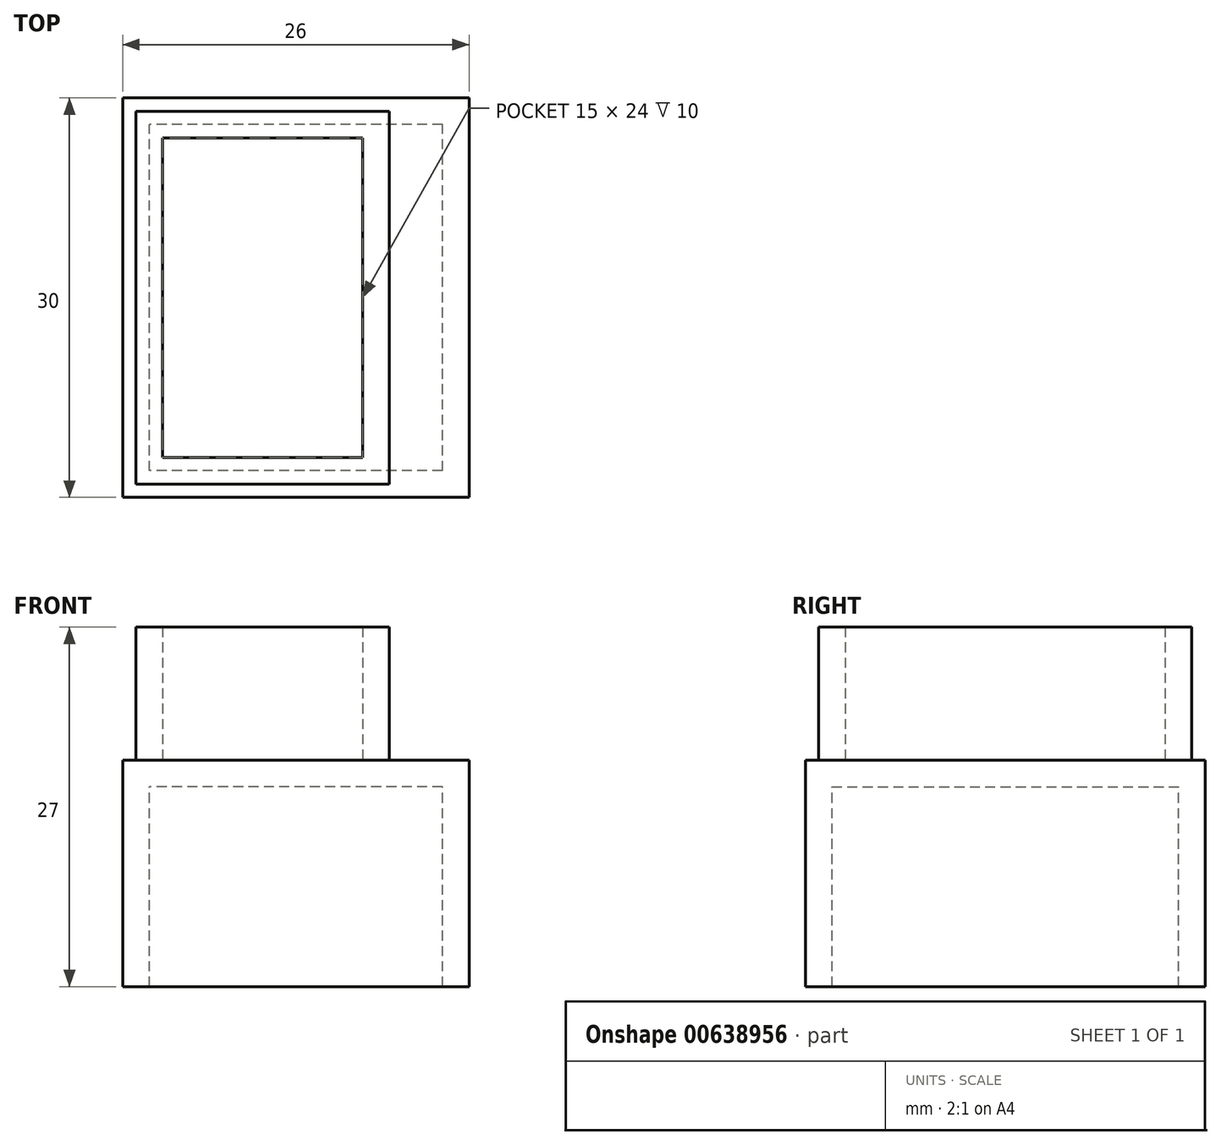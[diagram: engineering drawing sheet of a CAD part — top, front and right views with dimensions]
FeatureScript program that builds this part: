
annotation { "Feature Type Name" : "Feature", "Feature Type Description" : "" }
export const myFeature = defineFeature(function(context is Context, id is Id, definition is map)
    precondition{}
    {
        {
            var Q0;
            Q0=qCreatedBy(makeId("Top.planeOp"),FACE);
            var sketch = newSketch(context, id + "F0", { "sketchPlane" : qUnion([Q0])});
            skLineSegment(sketch, "E0.bottom", {"start": v(11, -13) * mm, "end": v(-11, -13) * mm});
            skLineSegment(sketch, "E0.top", {"start": v(11, 13) * mm, "end": v(-11, 13) * mm});
            skLineSegment(sketch, "E0.left", {"start": v(11, -13) * mm, "end": v(11, 13) * mm});
            skLineSegment(sketch, "E0.right", {"start": v(-11, -13) * mm, "end": v(-11, 13) * mm});
            skPoint(sketch, "E0.middle", {"position": v(0, 0) * mm});
            skLineSegment(sketch, "E1.bottom", {"start": v(13, -15) * mm, "end": v(-13, -15) * mm});
            skLineSegment(sketch, "E1.top", {"start": v(13, 15) * mm, "end": v(-13, 15) * mm});
            skLineSegment(sketch, "E1.left", {"start": v(13, -15) * mm, "end": v(13, 15) * mm});
            skLineSegment(sketch, "E1.right", {"start": v(-13, -15) * mm, "end": v(-13, 15) * mm});
            skSolve(sketch);
        }
        {
            var Q0;
            Q0=makeQuery(id+"F0.imprint","IMPRINT",FACE,{"disambiguationData":[TD([[makeQuery(id+"F0.imprint","IMPRINT",EDGE,{"derivedFrom":sQuery(id+"F0.wireOp",EDGE,"E0.bottom")}),1.0]])]});
            extrude(context, id + "F1", {"entities" : qUnion([Q0]), "oppositeDirection" : true, "depth" : 17 * mm, "offsetDistance" : 25 * mm});
        }
        {
            var Q0;
            Q0=makeQuery(id+"F0.imprint","IMPRINT",FACE,{"disambiguationData":[TD([[makeQuery(id+"F0.imprint","IMPRINT",EDGE,{"derivedFrom":sQuery(id+"F0.wireOp",EDGE,"E0.bottom")}),-1.0]])]});
            extrude(context, id + "F2", {"entities" : qUnion([Q0]), "operationType" : NewBodyOperationType.ADD, "oppositeDirection" : true, "depth" : 2 * mm, "offsetDistance" : 25 * mm});
        }
        {
            var Q0;
            Q0=qCreatedBy(makeId("Top.planeOp"),FACE);
            var sketch = newSketch(context, id + "F3", { "sketchPlane" : qUnion([Q0])});
            skLineSegment(sketch, "E2.bottom", {"start": v(-12, 14) * mm, "end": v(7, 14) * mm});
            skLineSegment(sketch, "E2.top", {"start": v(-12, -14) * mm, "end": v(7, -14) * mm});
            skLineSegment(sketch, "E2.left", {"start": v(-12, 14) * mm, "end": v(-12, -14) * mm});
            skLineSegment(sketch, "E2.right", {"start": v(7, 14) * mm, "end": v(7, -14) * mm});
            skLineSegment(sketch, "E3.bottom", {"start": v(-10, 12) * mm, "end": v(5, 12) * mm});
            skLineSegment(sketch, "E3.top", {"start": v(-10, -12) * mm, "end": v(5, -12) * mm});
            skLineSegment(sketch, "E3.left", {"start": v(-10, 12) * mm, "end": v(-10, -12) * mm});
            skLineSegment(sketch, "E3.right", {"start": v(5, 12) * mm, "end": v(5, -12) * mm});
            skSolve(sketch);
        }
        {
            var Q0;
            Q0 = qSketchRegion(id + "F3", true);
            extrude(context, id + "F4", {"entities" : qUnion([Q0]), "operationType" : NewBodyOperationType.ADD, "depth" : 10 * mm, "offsetDistance" : 25 * mm});
        }
    });
